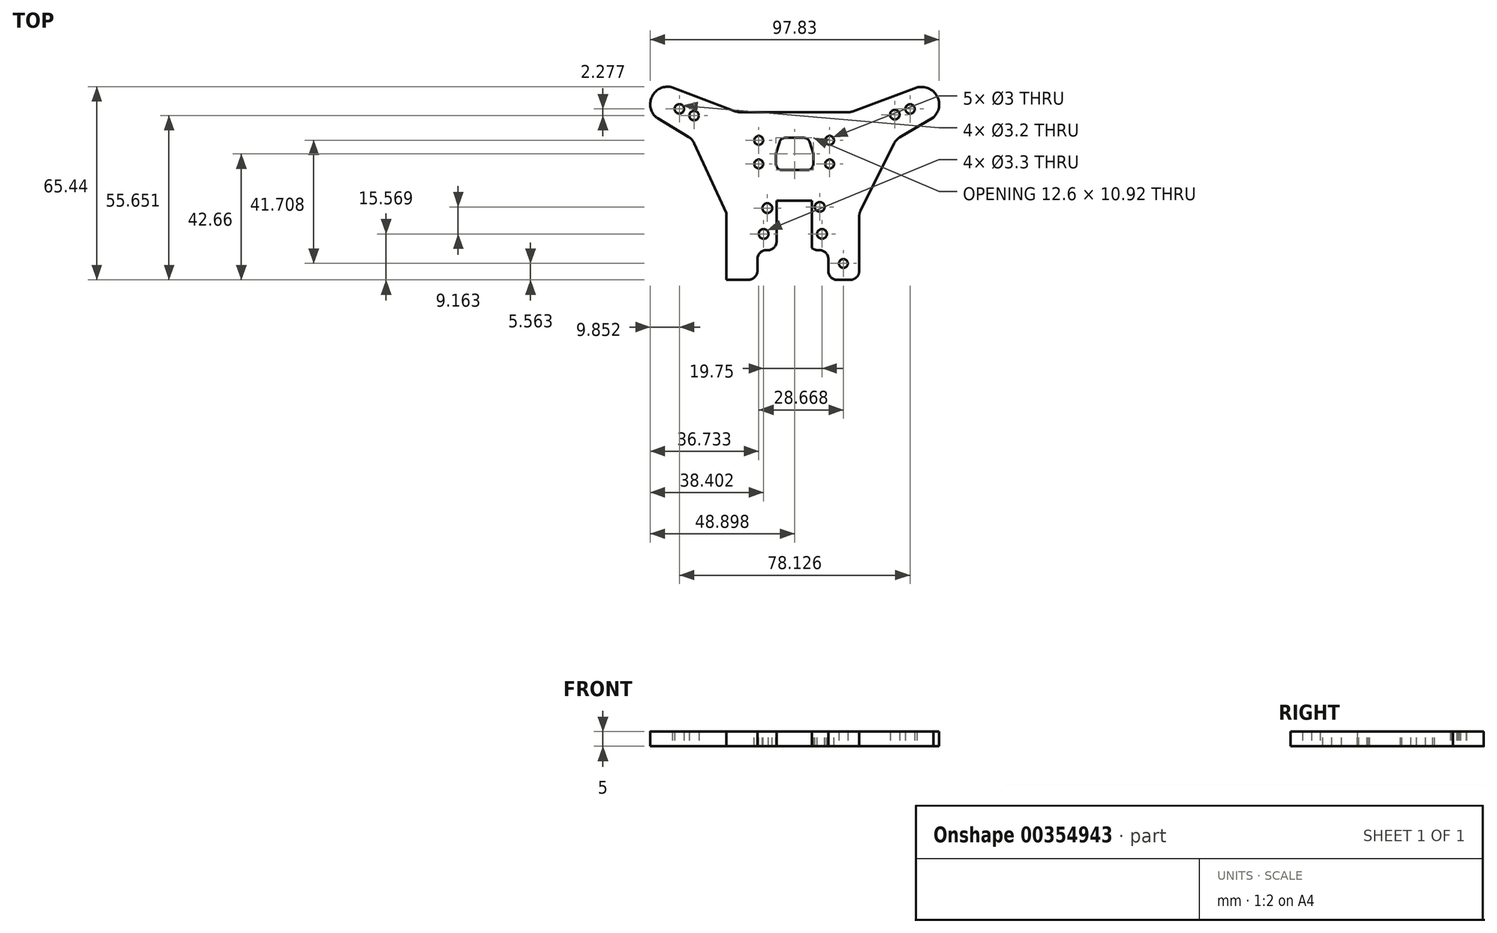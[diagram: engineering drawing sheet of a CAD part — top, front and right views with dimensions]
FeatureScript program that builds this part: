
annotation { "Feature Type Name" : "Feature", "Feature Type Description" : "" }
export const myFeature = defineFeature(function(context is Context, id is Id, definition is map)
    precondition{}
    {
        {
            var Q0;
            Q0=qCreatedBy(makeId("Top.planeOp"),FACE);
            var sketch = newSketch(context, id + "F0", { "sketchPlane" : qUnion([Q0])});
            skLineSegment(sketch, "E0.bottom", {"start": v(0, 0) * mm, "end": v(-10, 0.02) * mm});
            skLineSegment(sketch, "E1", {"start": v(-34, 0.07) * mm, "end": v(-34, 10.07) * mm});
            skLineSegment(sketch, "E2", {"start": v(-10, 0.02) * mm, "end": v(-10, 10.07) * mm});
            skLineSegment(sketch, "E3", {"start": v(-34, 10.07) * mm, "end": v(-27.5, 10.07) * mm});
            skLineSegment(sketch, "E4.left", {"start": v(-27.5, 10.07) * mm, "end": v(-27.5, 22.57) * mm});
            skLineSegment(sketch, "E4.right", {"start": v(-16.5, 10.07) * mm, "end": v(-16.5, 26.38) * mm});
            skLineSegment(sketch, "E5.trimOffspring", {"start": v(-16.5, 10.07) * mm, "end": v(-10, 10.07) * mm});
            skLineSegment(sketch, "E6", {"start": v(12.95, 47.55) * mm, "end": v(0.45, 22.5) * mm});
            skCircle(sketch, "E7", {"center": v(-4.89, 5.56) * mm, "radius": 1.5 * mm});
            skLineSegment(sketch, "E8", {"start": v(-27.5, 26.38) * mm, "end": v(-16.5, 26.38) * mm});
            skLineSegment(sketch, "E9", {"start": v(-27.5, 22.57) * mm, "end": v(-27.5, 26.38) * mm});
            skLineSegment(sketch, "E10", {"start": v(-40.55, 56.79) * mm, "end": v(-2.5, 56.79) * mm});
            skPoint(sketch, "E11.end.orphan", {"position": v(-74.59, 55.13) * mm});
            skPoint(sketch, "E12.end.orphan", {"position": v(-74.59, 47.47) * mm});
            skPoint(sketch, "E13.end.orphan", {"position": v(31.73, 55.13) * mm});
            skLineSegment(sketch, "E14", {"start": v(-40.55, 56.79) * mm, "end": v(-62.78, 65.24) * mm});
            skPoint(sketch, "E15.end.orphan", {"position": v(-73.6, 50.9) * mm});
            skLineSegment(sketch, "E16", {"start": v(-2.5, 56.79) * mm, "end": v(19.95, 65.13) * mm});
            skLineSegment(sketch, "E17", {"start": v(-56.05, 47.64) * mm, "end": v(-68.42, 55.15) * mm});
            skLineSegment(sketch, "E18", {"start": v(12.95, 47.55) * mm, "end": v(25.53, 54.98) * mm});
            skPoint(sketch, "E19.start.orphan", {"position": v(-71.21, 61.31) * mm});
            skPoint(sketch, "E20.end.orphan", {"position": v(28.5, 61.31) * mm});
            skArc(sketch, "E21", {"start": v(-61.68, 64.82) * mm, "mid": v(-69.83, 61.8) * mm, "end": v(-66.3, 53.87) * mm});
            skArc(sketch, "E22", {"start": v(23.59, 53.83) * mm, "mid": v(27.1, 61.66) * mm, "end": v(19.11, 64.82) * mm});
            skPoint(sketch, "E23.center.orphan", {"position": v(31.34, 64.47) * mm});
            skPoint(sketch, "E23.start.orphan", {"position": v(34.22, 60.1) * mm});
            skPoint(sketch, "E24.orphan", {"position": v(28.5, 68.31) * mm});
            skPoint(sketch, "E25.center.orphan", {"position": v(-73.96, 64.38) * mm});
            skPoint(sketch, "E25.start.orphan", {"position": v(-70.84, 68.3) * mm});
            skPoint(sketch, "E26.orphan", {"position": v(-76.56, 60.1) * mm});
            skLineSegment(sketch, "E27", {"start": v(-43.55, 22.58) * mm, "end": v(-43.55, 0) * mm});
            skLineSegment(sketch, "E28", {"start": v(-43.55, 0) * mm, "end": v(-34, 0.07) * mm});
            skPoint(sketch, "E29.orphan", {"position": v(-44, 0.09) * mm});
            skLineSegment(sketch, "E30", {"start": v(0.45, 22.5) * mm, "end": v(0.45, 0) * mm});
            skLineSegment(sketch, "E31", {"start": v(0.45, 0) * mm, "end": v(0, 0) * mm});
            skCircle(sketch, "E32", {"center": v(-60.44, 57.93) * mm, "radius": 1.6 * mm});
            skCircle(sketch, "E33", {"center": v(17.69, 57.89) * mm, "radius": 1.6 * mm});
            skCircle(sketch, "E34", {"center": v(-55.43, 55.65) * mm, "radius": 1.6 * mm});
            skCircle(sketch, "E35", {"center": v(12.53, 55.97) * mm, "radius": 1.6 * mm});
            skLineSegment(sketch, "E36", {"start": v(-44.5, 22.58) * mm, "end": v(-44.5, 0) * mm});
            skLineSegment(sketch, "E37", {"start": v(-44.5, 0) * mm, "end": v(-43.55, 0) * mm});
            skLineSegment(sketch, "E38", {"start": v(-56.05, 47.64) * mm, "end": v(-44.5, 22.58) * mm});
            skPoint(sketch, "E39.center.orphan", {"position": v(-38.89, 9.81) * mm});
            skPoint(sketch, "E40.center.orphan", {"position": v(-38.89, 5.56) * mm});
            skPoint(sketch, "E41.center.orphan", {"position": v(-4.89, 9.81) * mm});
            skSolve(sketch);
        }
        {
            var Q0;
            Q0=makeQuery(id+"F0.imprint","IMPRINT",FACE,{"disambiguationData":[TD([[makeQuery(id+"F0.imprint","IMPRINT",EDGE,{"derivedFrom":sQuery(id+"F0.wireOp",EDGE,"E0.bottom")}),-1.0]])]});
            extrude(context, id + "F1", {"entities" : qUnion([Q0]), "depth" : 5 * mm});
        }
        {
            var Q0;
            Q0=makeQuery(id+"F1.opExtrude","SWEPT_EDGE",EDGE,{"disambiguationData":[OSD([sQuery(id+"F0.wireOp",EDGE,"E3"),sQuery(id+"F0.wireOp",EDGE,"E4.left")])]});
            var Q1;
            Q1=makeQuery(id+"F1.opExtrude","SWEPT_EDGE",EDGE,{"disambiguationData":[OSD([sQuery(id+"F0.wireOp",EDGE,"E1"),sQuery(id+"F0.wireOp",EDGE,"E3")])]});
            var Q2;
            Q2=makeQuery(id+"F1.opExtrude","SWEPT_EDGE",EDGE,{"disambiguationData":[OSD([sQuery(id+"F0.wireOp",EDGE,"E4.right"),sQuery(id+"F0.wireOp",EDGE,"E5.trimOffspring")])]});
            var Q3;
            Q3=makeQuery(id+"F1.opExtrude","SWEPT_EDGE",EDGE,{"disambiguationData":[OSD([sQuery(id+"F0.wireOp",EDGE,"E2"),sQuery(id+"F0.wireOp",EDGE,"E5.trimOffspring")])]});
            var Q4;
            Q4=makeQuery(id+"F1.opExtrude","SWEPT_EDGE",EDGE,{"disambiguationData":[OSD([sQuery(id+"F0.wireOp",EDGE,"E0.bottom"),sQuery(id+"F0.wireOp",EDGE,"E2")])]});
            var Q5;
            Q5=makeQuery(id+"F1.opExtrude","SWEPT_EDGE",EDGE,{"disambiguationData":[OSD([sQuery(id+"F0.wireOp",EDGE,"E1"),sQuery(id+"F0.wireOp",EDGE,"E28")])]});
            var Q6;
            Q6=makeQuery(id+"F1.opExtrude","SWEPT_EDGE",EDGE,{"disambiguationData":[OSD([sQuery(id+"F0.wireOp",EDGE,"E27"),sQuery(id+"F0.wireOp",EDGE,"E28")])]});
            var Q7;
            Q7=makeQuery(id+"F1.opExtrude","SWEPT_EDGE",EDGE,{"disambiguationData":[OSD([sQuery(id+"F0.wireOp",EDGE,"E30"),sQuery(id+"F0.wireOp",EDGE,"E31")])]});
            fillet(context, id + "F2", {"entities" : qUnion([Q0, Q1, Q2, Q3, Q4, Q5, Q6, Q7]), "radius" : 3 * mm, "tangentPropagation" : true, "allowEdgeOverflow" : false});
        }
        {
            var Q0;
            Q0=makeQuery(id+"F1.opExtrude","SWEPT_EDGE",EDGE,{"disambiguationData":[OSD([sQuery(id+"F0.wireOp",EDGE,"E8"),sQuery(id+"F0.wireOp",EDGE,"E9")])]});
            var Q1;
            Q1=makeQuery(id+"F1.opExtrude","SWEPT_EDGE",EDGE,{"disambiguationData":[OSD([sQuery(id+"F0.wireOp",EDGE,"E4.right"),sQuery(id+"F0.wireOp",EDGE,"E8")])]});
            fillet(context, id + "F3", {"entities" : qUnion([Q0, Q1]), "radius" : 2 * mm, "tangentPropagation" : true, "allowEdgeOverflow" : false});
        }
        {
            var Q0;
            Q0=makeQuery(id+"F1.opExtrude","SWEPT_EDGE",EDGE,{"disambiguationData":[OSD([sQuery(id+"F0.wireOp",EDGE,"OJ4ICmkx-gYxG-Y3OP-QNAm-WvVsQIgY6rMI"),sQuery(id+"F0.wireOp",EDGE,"E27")])]});
            var Q1;
            Q1=makeQuery(id+"F1.opExtrude","SWEPT_EDGE",EDGE,{"disambiguationData":[OSD([sQuery(id+"F0.wireOp",EDGE,"E6"),sQuery(id+"F0.wireOp",EDGE,"E30")])]});
            fillet(context, id + "F4", {"entities" : qUnion([Q0, Q1]), "radius" : 5 * mm, "tangentPropagation" : true, "allowEdgeOverflow" : false});
        }
        {
            var Q0;
            Q0=makeQuery(id+"F1.opExtrude","SWEPT_EDGE",EDGE,{"disambiguationData":[OSD([sQuery(id+"F0.wireOp",EDGE,"OJ4ICmkx-gYxG-Y3OP-QNAm-WvVsQIgY6rMI"),sQuery(id+"F0.wireOp",EDGE,"E17")])]});
            var Q1;
            Q1=makeQuery(id+"F1.opExtrude","SWEPT_EDGE",EDGE,{"disambiguationData":[OSD([sQuery(id+"F0.wireOp",EDGE,"E6"),sQuery(id+"F0.wireOp",EDGE,"E18")])]});
            var Q2;
            Q2=makeQuery(id+"F1.opExtrude","SWEPT_EDGE",EDGE,{"disambiguationData":[OSD([sQuery(id+"F0.wireOp",EDGE,"E10"),sQuery(id+"F0.wireOp",EDGE,"E16")])]});
            var Q3;
            Q3=makeQuery(id+"F1.opExtrude","SWEPT_EDGE",EDGE,{"disambiguationData":[OSD([sQuery(id+"F0.wireOp",EDGE,"E10"),sQuery(id+"F0.wireOp",EDGE,"E14")])]});
            fillet(context, id + "F5", {"entities" : qUnion([Q0, Q1, Q2, Q3]), "radius" : 5 * mm, "tangentPropagation" : true, "allowEdgeOverflow" : false});
        }
        {
            var Q0;
            Q0=makeQuery(id+"F1.opExtrude","CAP_FACE",FACE,{"disambiguationData":[OSD([sQuery(id+"F0.wireOp",EDGE,"E0.bottom"),sQuery(id+"F0.wireOp",EDGE,"E1"),sQuery(id+"F0.wireOp",EDGE,"E2"),sQuery(id+"F0.wireOp",EDGE,"E3"),sQuery(id+"F0.wireOp",EDGE,"E4.left"),sQuery(id+"F0.wireOp",EDGE,"E4.right"),sQuery(id+"F0.wireOp",EDGE,"E5.trimOffspring"),sQuery(id+"F0.wireOp",EDGE,"OJ4ICmkx-gYxG-Y3OP-QNAm-WvVsQIgY6rMI"),sQuery(id+"F0.wireOp",EDGE,"E6"),sQuery(id+"F0.wireOp",EDGE,"E40"),sQuery(id+"F0.wireOp",EDGE,"E7"),sQuery(id+"F0.wireOp",EDGE,"E8"),sQuery(id+"F0.wireOp",EDGE,"E9"),sQuery(id+"F0.wireOp",EDGE,"E10"),sQuery(id+"F0.wireOp",EDGE,"E14"),sQuery(id+"F0.wireOp",EDGE,"E16"),sQuery(id+"F0.wireOp",EDGE,"E17"),sQuery(id+"F0.wireOp",EDGE,"E18"),sQuery(id+"F0.wireOp",EDGE,"E21"),sQuery(id+"F0.wireOp",EDGE,"E22"),sQuery(id+"F0.wireOp",EDGE,"E27"),sQuery(id+"F0.wireOp",EDGE,"E28"),sQuery(id+"F0.wireOp",EDGE,"E30"),sQuery(id+"F0.wireOp",EDGE,"E31"),sQuery(id+"F0.wireOp",EDGE,"E32"),sQuery(id+"F0.wireOp",EDGE,"E33"),sQuery(id+"F0.wireOp",EDGE,"E34"),sQuery(id+"F0.wireOp",EDGE,"E35"),sQuery(id+"F0.wireOp",EDGE,"E39"),sQuery(id+"F0.wireOp",EDGE,"E41")])],"isStart":false});
            var sketch = newSketch(context, id + "F6", { "sketchPlane" : qUnion([Q0])});
            skCircle(sketch, "E42", {"center": v(-33.56, 47.27) * mm, "radius": 1.5 * mm});
            skCircle(sketch, "E43", {"center": v(-9.56, 47.27) * mm, "radius": 1.5 * mm});
            skCircle(sketch, "E44", {"center": v(-33.56, 39.27) * mm, "radius": 1.5 * mm});
            skCircle(sketch, "E45", {"center": v(-9.56, 39.27) * mm, "radius": 1.5 * mm});
            skPoint(sketch, "E46.start.orphan", {"position": v(-3.4, 30.4) * mm});
            skLineSegment(sketch, "E47", {"start": v(-43.55, 15.64) * mm, "end": v(-27.5, 15.64) * mm});
            skPoint(sketch, "E48.oppositeSnap0", {"position": v(-15.62, 10.94) * mm});
            skLineSegment(sketch, "E48.bottom", {"start": v(-27.5, 24.38) * mm, "end": v(-15.62, 24.38) * mm});
            skLineSegment(sketch, "E48.top", {"start": v(-27.5, 8.54) * mm, "end": v(-15.62, 8.54) * mm});
            skLineSegment(sketch, "E48.left", {"start": v(-27.5, 24.38) * mm, "end": v(-27.5, 8.54) * mm});
            skLineSegment(sketch, "E48.right", {"start": v(-15.62, 24.38) * mm, "end": v(-15.62, 8.54) * mm});
            skSolve(sketch);
        }
        {
            var Q0;
            Q0=makeQuery(id+"F6.imprint","IMPRINT",FACE,{"disambiguationData":[TD([[makeQuery(id+"F6.imprint","IMPRINT",EDGE,{"derivedFrom":sQuery(id+"F6.wireOp",EDGE,"E42")}),1.0]])]});
            var Q1;
            Q1=makeQuery(id+"F6.imprint","IMPRINT",FACE,{"disambiguationData":[TD([[makeQuery(id+"F6.imprint","IMPRINT",EDGE,{"derivedFrom":sQuery(id+"F6.wireOp",EDGE,"E44")}),1.0]])]});
            var Q2;
            Q2=makeQuery(id+"F6.imprint","IMPRINT",FACE,{"disambiguationData":[TD([[makeQuery(id+"F6.imprint","IMPRINT",EDGE,{"derivedFrom":sQuery(id+"F6.wireOp",EDGE,"E45")}),1.0]])]});
            var Q3;
            Q3=makeQuery(id+"F6.imprint","IMPRINT",FACE,{"disambiguationData":[TD([[makeQuery(id+"F6.imprint","IMPRINT",EDGE,{"derivedFrom":sQuery(id+"F6.wireOp",EDGE,"E43")}),1.0]])]});
            var Q4;
            Q4 = qConstructionFilter(qBodyType(qCreatedBy(id + "F6" ,EDGE), BodyType.WIRE), ConstructionObject.NO);
            extrude(context, id + "F7", {"entities" : qUnion([Q0, Q1, Q2, Q3]), "operationType" : NewBodyOperationType.REMOVE, "surfaceEntities" : qUnion([Q4]), "oppositeDirection" : true, "depth" : 25 * mm});
        }
        {
            var Q0;
            Q0=makeQuery(id+"F1.opExtrude","CAP_FACE",FACE,{"disambiguationData":[OSD([sQuery(id+"F0.wireOp",EDGE,"E0.bottom"),sQuery(id+"F0.wireOp",EDGE,"E1"),sQuery(id+"F0.wireOp",EDGE,"E2"),sQuery(id+"F0.wireOp",EDGE,"E3"),sQuery(id+"F0.wireOp",EDGE,"E4.left"),sQuery(id+"F0.wireOp",EDGE,"E4.right"),sQuery(id+"F0.wireOp",EDGE,"E5.trimOffspring"),sQuery(id+"F0.wireOp",EDGE,"OJ4ICmkx-gYxG-Y3OP-QNAm-WvVsQIgY6rMI"),sQuery(id+"F0.wireOp",EDGE,"E6"),sQuery(id+"F0.wireOp",EDGE,"E40"),sQuery(id+"F0.wireOp",EDGE,"E7"),sQuery(id+"F0.wireOp",EDGE,"E8"),sQuery(id+"F0.wireOp",EDGE,"E9"),sQuery(id+"F0.wireOp",EDGE,"E10"),sQuery(id+"F0.wireOp",EDGE,"E14"),sQuery(id+"F0.wireOp",EDGE,"E16"),sQuery(id+"F0.wireOp",EDGE,"E17"),sQuery(id+"F0.wireOp",EDGE,"E18"),sQuery(id+"F0.wireOp",EDGE,"E21"),sQuery(id+"F0.wireOp",EDGE,"E22"),sQuery(id+"F0.wireOp",EDGE,"E27"),sQuery(id+"F0.wireOp",EDGE,"E28"),sQuery(id+"F0.wireOp",EDGE,"E30"),sQuery(id+"F0.wireOp",EDGE,"E31"),sQuery(id+"F0.wireOp",EDGE,"E32"),sQuery(id+"F0.wireOp",EDGE,"E33"),sQuery(id+"F0.wireOp",EDGE,"E34"),sQuery(id+"F0.wireOp",EDGE,"E35"),sQuery(id+"F0.wireOp",EDGE,"E39"),sQuery(id+"F0.wireOp",EDGE,"E41")])],"isStart":false});
            var sketch = newSketch(context, id + "F8", { "sketchPlane" : qUnion([Q0])});
            skLineSegment(sketch, "E49.bottom", {"start": v(-26.1, 48.12) * mm, "end": v(-16.77, 48.12) * mm});
            skLineSegment(sketch, "E49.top", {"start": v(-27.7, 37.2) * mm, "end": v(-15.1, 37.2) * mm});
            skLineSegment(sketch, "E49.left", {"start": v(-27.7, 42.66) * mm, "end": v(-27.7, 37.2) * mm});
            skLineSegment(sketch, "E49.right", {"start": v(-15.1, 42.66) * mm, "end": v(-15.1, 37.2) * mm});
            skLineSegment(sketch, "E50.left", {"start": v(-26.1, 42.66) * mm, "end": v(-26.1, 42.58) * mm});
            skLineSegment(sketch, "E50.right", {"start": v(-16.77, 42.66) * mm, "end": v(-16.77, 42.58) * mm});
            skLineSegment(sketch, "E51", {"start": v(-26.1, 48.12) * mm, "end": v(-27.7, 42.66) * mm});
            skLineSegment(sketch, "E52", {"start": v(-15.1, 42.66) * mm, "end": v(-16.77, 48.12) * mm});
            skPoint(sketch, "E53.orphan", {"position": v(-27.7, 48.12) * mm});
            skPoint(sketch, "E54.orphan", {"position": v(-15.1, 48.12) * mm});
            skSolve(sketch);
        }
        {
            var Q0;
            Q0 = qSketchRegion(id + "F8", true);
            extrude(context, id + "F9", {"entities" : qUnion([Q0]), "operationType" : NewBodyOperationType.REMOVE, "oppositeDirection" : true, "depth" : 25 * mm});
        }
        {
            var Q0;
            Q0=makeQuery(id+"F9.boolean.opBoolean","COPY",EDGE,{"derivedFrom":makeQuery(id+"F9.opExtrude","SWEPT_EDGE",EDGE,{"disambiguationData":[OSD([sQuery(id+"F8.wireOp",EDGE,"E49.bottom"),sQuery(id+"F8.wireOp",EDGE,"E51")])]})});
            var Q1;
            Q1=makeQuery(id+"F9.boolean.opBoolean","COPY",EDGE,{"derivedFrom":makeQuery(id+"F9.opExtrude","SWEPT_EDGE",EDGE,{"disambiguationData":[OSD([sQuery(id+"F8.wireOp",EDGE,"E49.bottom"),sQuery(id+"F8.wireOp",EDGE,"E52")])]})});
            var Q2;
            Q2=makeQuery(id+"F9.boolean.opBoolean","COPY",EDGE,{"derivedFrom":makeQuery(id+"F9.opExtrude","SWEPT_EDGE",EDGE,{"disambiguationData":[OSD([sQuery(id+"F8.wireOp",EDGE,"E49.top"),sQuery(id+"F8.wireOp",EDGE,"E49.left")])]})});
            var Q3;
            Q3=makeQuery(id+"F9.boolean.opBoolean","COPY",EDGE,{"derivedFrom":makeQuery(id+"F9.opExtrude","SWEPT_EDGE",EDGE,{"disambiguationData":[OSD([sQuery(id+"F8.wireOp",EDGE,"E49.top"),sQuery(id+"F8.wireOp",EDGE,"E49.right")])]})});
            fillet(context, id + "F10", {"entities" : qUnion([Q0, Q1, Q2, Q3]), "radius" : 2 * mm, "tangentPropagation" : true, "allowEdgeOverflow" : false});
        }
        {
            var Q0;
            Q0=makeQuery(id+"F1.opExtrude","CAP_FACE",FACE,{"disambiguationData":[OSD([sQuery(id+"F0.wireOp",EDGE,"E0.bottom"),sQuery(id+"F0.wireOp",EDGE,"E1"),sQuery(id+"F0.wireOp",EDGE,"E2"),sQuery(id+"F0.wireOp",EDGE,"E3"),sQuery(id+"F0.wireOp",EDGE,"E4.left"),sQuery(id+"F0.wireOp",EDGE,"E4.right"),sQuery(id+"F0.wireOp",EDGE,"E5.trimOffspring"),sQuery(id+"F0.wireOp",EDGE,"OJ4ICmkx-gYxG-Y3OP-QNAm-WvVsQIgY6rMI"),sQuery(id+"F0.wireOp",EDGE,"E6"),sQuery(id+"F0.wireOp",EDGE,"E40"),sQuery(id+"F0.wireOp",EDGE,"E7"),sQuery(id+"F0.wireOp",EDGE,"E8"),sQuery(id+"F0.wireOp",EDGE,"E9"),sQuery(id+"F0.wireOp",EDGE,"E10"),sQuery(id+"F0.wireOp",EDGE,"E14"),sQuery(id+"F0.wireOp",EDGE,"E16"),sQuery(id+"F0.wireOp",EDGE,"E17"),sQuery(id+"F0.wireOp",EDGE,"E18"),sQuery(id+"F0.wireOp",EDGE,"E21"),sQuery(id+"F0.wireOp",EDGE,"E22"),sQuery(id+"F0.wireOp",EDGE,"E27"),sQuery(id+"F0.wireOp",EDGE,"E28"),sQuery(id+"F0.wireOp",EDGE,"E30"),sQuery(id+"F0.wireOp",EDGE,"E31"),sQuery(id+"F0.wireOp",EDGE,"E32"),sQuery(id+"F0.wireOp",EDGE,"E33"),sQuery(id+"F0.wireOp",EDGE,"E34"),sQuery(id+"F0.wireOp",EDGE,"E35"),sQuery(id+"F0.wireOp",EDGE,"E39"),sQuery(id+"F0.wireOp",EDGE,"E41")])],"isStart":false});
            var sketch = newSketch(context, id + "F11", { "sketchPlane" : qUnion([Q0])});
            skLineSegment(sketch, "E55", {"start": v(-38.89, 9.81) * mm, "end": v(-38.89, 29.32) * mm});
            skLineSegment(sketch, "E56", {"start": v(-4.89, 9.81) * mm, "end": v(-4.89, 30.45) * mm});
            skCircle(sketch, "E57", {"center": v(-31.89, 15.57) * mm, "radius": 1.65 * mm});
            skCircle(sketch, "E58", {"center": v(-12.14, 15.57) * mm, "radius": 1.65 * mm});
            skCircle(sketch, "E59", {"center": v(-30.64, 24.32) * mm, "radius": 1.65 * mm});
            skCircle(sketch, "E60", {"center": v(-12.9, 24.73) * mm, "radius": 1.65 * mm});
            skLineSegment(sketch, "E61", {"start": v(-30.64, 24.32) * mm, "end": v(-8.57, 24.32) * mm});
            skSolve(sketch);
        }
        {
            var Q0;
            Q0 = qSketchRegion(id + "F11", true);
            extrude(context, id + "F12", {"entities" : qUnion([Q0]), "operationType" : NewBodyOperationType.REMOVE, "oppositeDirection" : true, "depth" : 25 * mm});
        }
        {
            var Q0;
            Q0=makeQuery(id+"F1.opExtrude","CAP_FACE",FACE,{"disambiguationData":[OSD([sQuery(id+"F0.wireOp",EDGE,"E0.bottom"),sQuery(id+"F0.wireOp",EDGE,"E1"),sQuery(id+"F0.wireOp",EDGE,"E2"),sQuery(id+"F0.wireOp",EDGE,"E3"),sQuery(id+"F0.wireOp",EDGE,"E4.left"),sQuery(id+"F0.wireOp",EDGE,"E4.right"),sQuery(id+"F0.wireOp",EDGE,"E5.trimOffspring"),sQuery(id+"F0.wireOp",EDGE,"OJ4ICmkx-gYxG-Y3OP-QNAm-WvVsQIgY6rMI"),sQuery(id+"F0.wireOp",EDGE,"E6"),sQuery(id+"F0.wireOp",EDGE,"E40"),sQuery(id+"F0.wireOp",EDGE,"E7"),sQuery(id+"F0.wireOp",EDGE,"E8"),sQuery(id+"F0.wireOp",EDGE,"E9"),sQuery(id+"F0.wireOp",EDGE,"E10"),sQuery(id+"F0.wireOp",EDGE,"E14"),sQuery(id+"F0.wireOp",EDGE,"E16"),sQuery(id+"F0.wireOp",EDGE,"E17"),sQuery(id+"F0.wireOp",EDGE,"E18"),sQuery(id+"F0.wireOp",EDGE,"E21"),sQuery(id+"F0.wireOp",EDGE,"E22"),sQuery(id+"F0.wireOp",EDGE,"E27"),sQuery(id+"F0.wireOp",EDGE,"E28"),sQuery(id+"F0.wireOp",EDGE,"E30"),sQuery(id+"F0.wireOp",EDGE,"E31"),sQuery(id+"F0.wireOp",EDGE,"E32"),sQuery(id+"F0.wireOp",EDGE,"E33"),sQuery(id+"F0.wireOp",EDGE,"E34"),sQuery(id+"F0.wireOp",EDGE,"E35"),sQuery(id+"F0.wireOp",EDGE,"E39"),sQuery(id+"F0.wireOp",EDGE,"E41")])],"isStart":false});
            var sketch = newSketch(context, id + "F13", { "sketchPlane" : qUnion([Q0])});
            skLineSegment(sketch, "E62", {"start": v(-27.5, 24.38) * mm, "end": v(-27.5, 26.85) * mm});
            skLineSegment(sketch, "E63", {"start": v(-27.5, 26.85) * mm, "end": v(-16.1, 26.85) * mm});
            skLineSegment(sketch, "E64", {"start": v(-27.5, 26.85) * mm, "end": v(-15.6, 26.85) * mm});
            skLineSegment(sketch, "E65", {"start": v(-15.6, 26.85) * mm, "end": v(-15.6, 8.98) * mm});
            skLineSegment(sketch, "E66", {"start": v(-15.6, 8.98) * mm, "end": v(-27.5, 24.38) * mm});
            skSolve(sketch);
        }
        {
            var Q0;
            Q0 = qSketchRegion(id + "F13", true);
            extrude(context, id + "F14", {"entities" : qUnion([Q0]), "operationType" : NewBodyOperationType.REMOVE, "oppositeDirection" : true, "depth" : 25 * mm});
        }
    });
